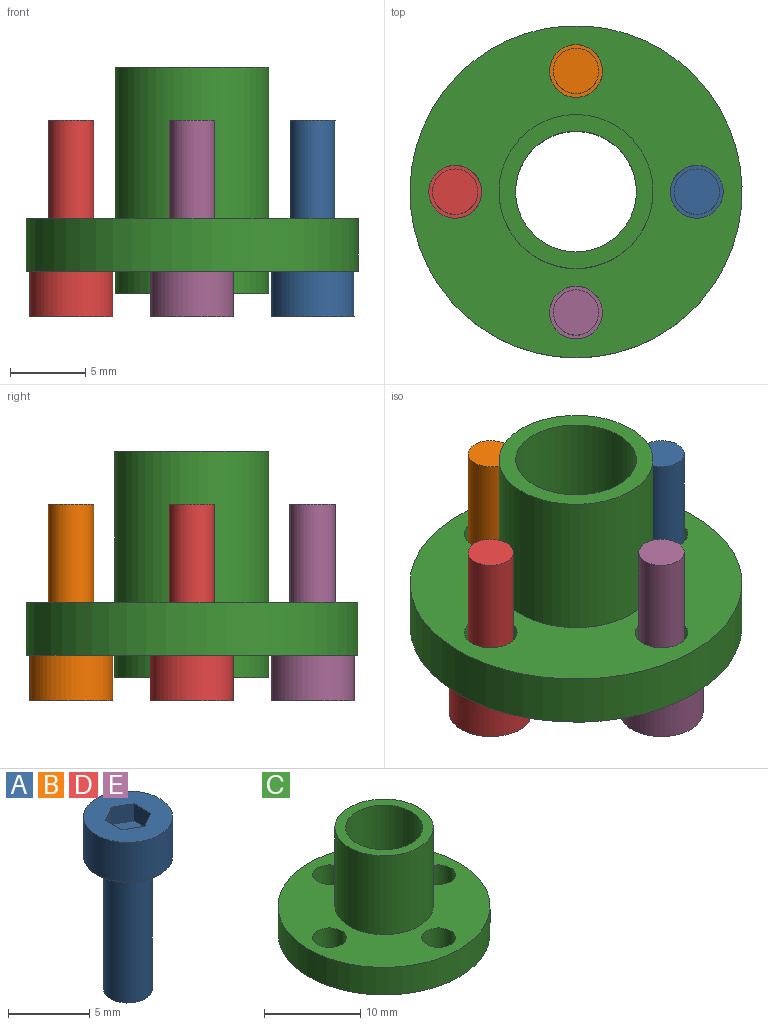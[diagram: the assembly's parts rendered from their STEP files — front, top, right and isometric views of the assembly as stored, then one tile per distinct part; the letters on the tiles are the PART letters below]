
ASSEMBLY  parts=5 mates=4
PART A: 12 faces, bbox 5.5x5.5x13 mm
  f0: plane 5.5x5.5mm, normal (0,0,1), area 18.3mm2, adj f2,f5,f6,f7,f8,f9,f10
  f1: plane 3x3mm, normal (0,0,-1), area 7.1mm2, adj f4
  f2: cylinder r=2.75mm len=5.5mm, axis (0,0,-1), area 51.8mm2, adj f0,f3
  f3: plane 5.5x5.5mm, normal (0,0,-1), area 16.7mm2, adj f2,f4
  f4: cylinder r=1.5mm len=10mm, axis (0,0,-1), area 94.2mm2, adj f1,f3
  f5: plane 1.3x1.25mm, normal (0.5,0.87,0), area 1.9mm2, adj f0,f6,f10,f11
  f6: plane 1.3x1.25mm, normal (-0.5,0.87,0), area 1.9mm2, adj f0,f5,f7,f11
  f7: plane 1.44x1.3mm, normal (-1,0,0), area 1.9mm2, adj f0,f6,f8,f11
  f8: plane 1.3x1.25mm, normal (-0.5,-0.87,0), area 1.9mm2, adj f0,f7,f9,f11
  f9: plane 1.3x1.25mm, normal (0.5,-0.87,0), area 1.9mm2, adj f0,f8,f10,f11
  f10: plane 1.44x1.3mm, normal (1,0,0), area 1.9mm2, adj f0,f5,f9,f11
  f11: plane 2.89x2.5mm, normal (0,0,1), area 5.4mm2, adj f5,f6,f7,f8,f9,f10
PART B: same geometry as A
PART C: 17 faces, bbox 22x22x15 mm
  f0: plane 10.2x10.2mm, normal (0,0,-1), area 23.6mm2, adj f7,f8
  f1: cylinder r=4mm len=14.7mm, axis (0,0,1), area 369.5mm2, adj f2,f8
  f2: plane 10.2x10.2mm, normal (0,0,1), area 31.4mm2, adj f1,f3
  f3: cylinder r=5.1mm len=10.2mm, axis (0,0,1), area 320.4mm2, adj f2,f4
  f4: plane 22x22mm, normal (0,0,1), area 259.9mm2, adj f3,f5,f9,f10,f11,f12
  f5: cylinder r=11mm len=22mm, axis (0,0,1), area 241.9mm2, adj f4,f6
  f6: plane 22x22mm, normal (0,0,-1), area 234.8mm2, adj f5,f7,f13,f14,f15,f16
  f7: cylinder r=5.1mm len=10.2mm, axis (0,0,1), area 48.1mm2, adj f0,f6
  f8: cone r=4.3mm half-angle=45deg, axis (0,0,-1), area 11.1mm2, adj f0,f1
  f9: cylinder r=1.75mm len=3.5mm, axis (0,0,-1), area 33mm2, adj f4,f15
  f10: cylinder r=1.75mm len=3.5mm, axis (0,0,-1), area 33mm2, adj f4,f16
  f11: cylinder r=1.75mm len=3.5mm, axis (0,0,-1), area 33mm2, adj f4,f13
  f12: cylinder r=1.75mm len=3.5mm, axis (0,0,-1), area 33mm2, adj f4,f14
  f13: cone r=1.75mm half-angle=45deg, axis (0,0,-1), area 8.9mm2, adj f6,f11
  f14: cone r=1.75mm half-angle=45deg, axis (0,0,-1), area 8.9mm2, adj f6,f12
  f15: cone r=1.75mm half-angle=45deg, axis (0,0,-1), area 8.9mm2, adj f6,f9
  f16: cone r=1.75mm half-angle=45deg, axis (0,0,-1), area 8.9mm2, adj f6,f10
PART D: same geometry as A
PART E: same geometry as A
PLACE A rot(axis=(-1,0,0),180deg) t=(3.67,-4.7,-9.3)mm
PLACE B rot(axis=(-1,0,0),180deg) t=(-4.33,3.3,-9.3)mm
PLACE C t=(-4.33,-4.7,4.2)mm
PLACE D rot(axis=(-1,0,0),180deg) t=(-12.33,-4.7,-9.3)mm
PLACE E rot(axis=(-1,0,0),180deg) t=(-4.33,-12.7,-9.3)mm
MATE fastened B.f2 <-> C.f16  axis (0,0,1) through (-4.33,3.3,-9.3)mm
MATE fastened A.f2 <-> C.f13  axis (0,0,1) through (3.67,-4.7,-9.3)mm
MATE fastened D.f2 <-> C.f15  axis (0,0,1) through (-12.33,-4.7,-9.3)mm
MATE fastened E.f2 <-> C.f14  axis (0,0,1) through (-4.33,-12.7,-9.3)mm
